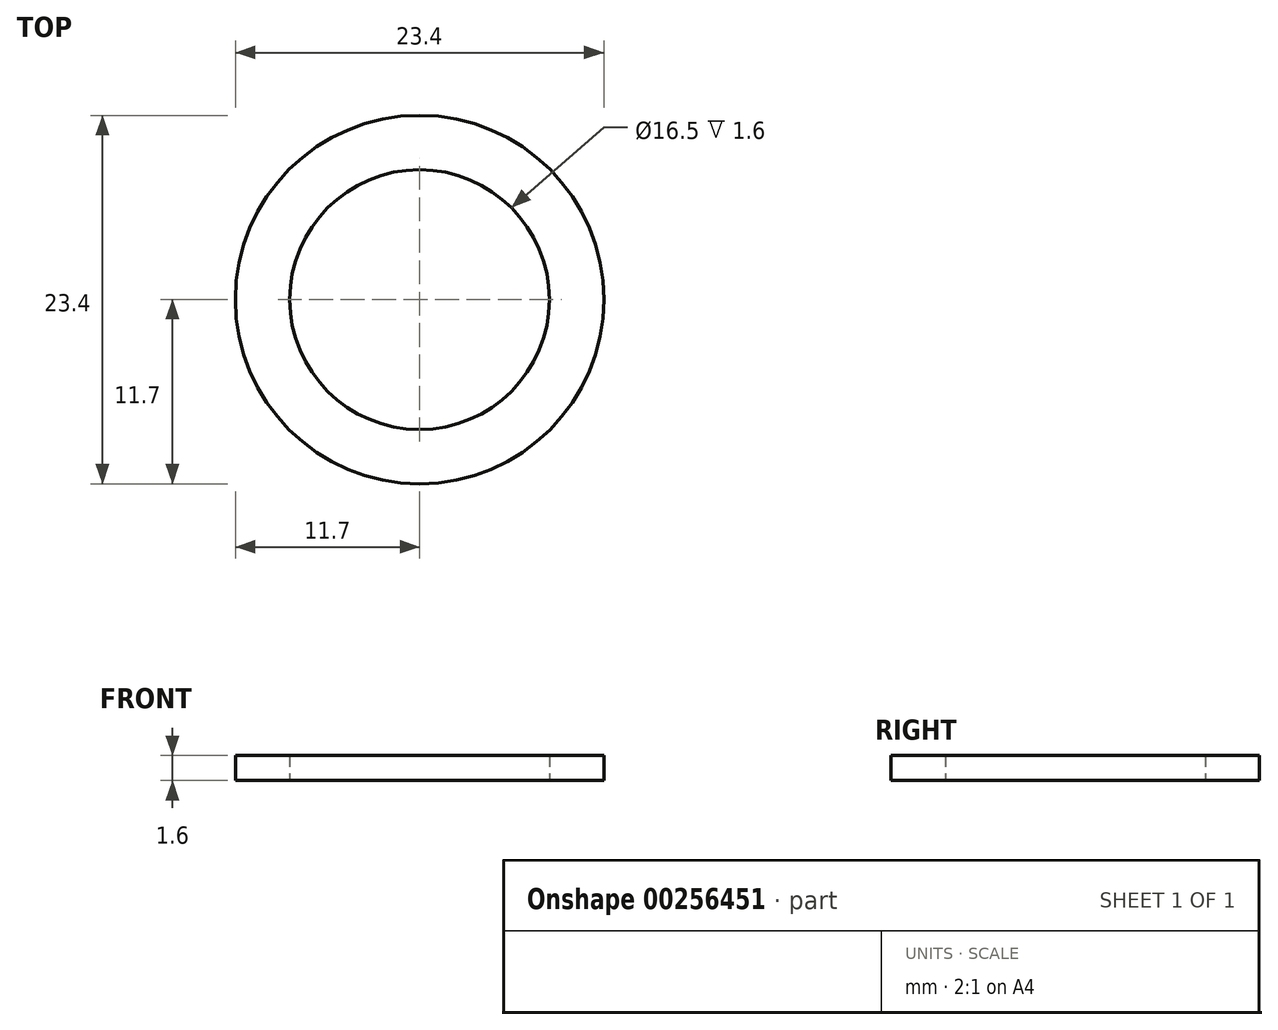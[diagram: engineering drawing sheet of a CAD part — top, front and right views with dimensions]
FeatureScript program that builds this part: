
annotation { "Feature Type Name" : "Feature", "Feature Type Description" : "" }
export const myFeature = defineFeature(function(context is Context, id is Id, definition is map)
    precondition{}
    {
        {
            var Q0;
            Q0=qCreatedBy(makeId("Top.planeOp"),FACE);
            var sketch = newSketch(context, id + "F0", { "sketchPlane" : qUnion([Q0])});
            skCircle(sketch, "E0", {"center": v(0, 0) * mm, "radius": 2.75 * mm});
            skCircle(sketch, "E1", {"center": v(0, 0) * mm, "radius": 3.9 * mm});
            skSolve(sketch);
        }
        {
            var Q0;
            Q0=makeQuery(id+"F0.imprint","IMPRINT",FACE,{"disambiguationData":[TD([[makeQuery(id+"F0.imprint","IMPRINT",EDGE,{"derivedFrom":sQuery(id+"F0.wireOp",EDGE,"E0")}),-1.0]])]});
            extrude(context, id + "F1", {"entities" : qUnion([Q0]), "depth" : (1.6 / 3) * mm, "offsetDistance" : 25 * mm});
        }
        {
            var Q0;
            Q0=makeQuery(id+"F1.opExtrude","SWEPT_BODY",BODY,{"disambiguationData":[OSD([sQuery(id+"F0.wireOp",EDGE,"E0"),sQuery(id+"F0.wireOp",EDGE,"E1")])]});
            var Q1;
            Q1=qCreatedBy(makeId("Origin.pointOp"),VERTEX);
            transform(context, id + "F2", {"entities" : qUnion([Q0]), "transformType" : TransformType.SCALE_UNIFORMLY, "scale" : 3, "makeCopy" : false, "scalePoint" : qUnion([Q1])});
        }
    });
